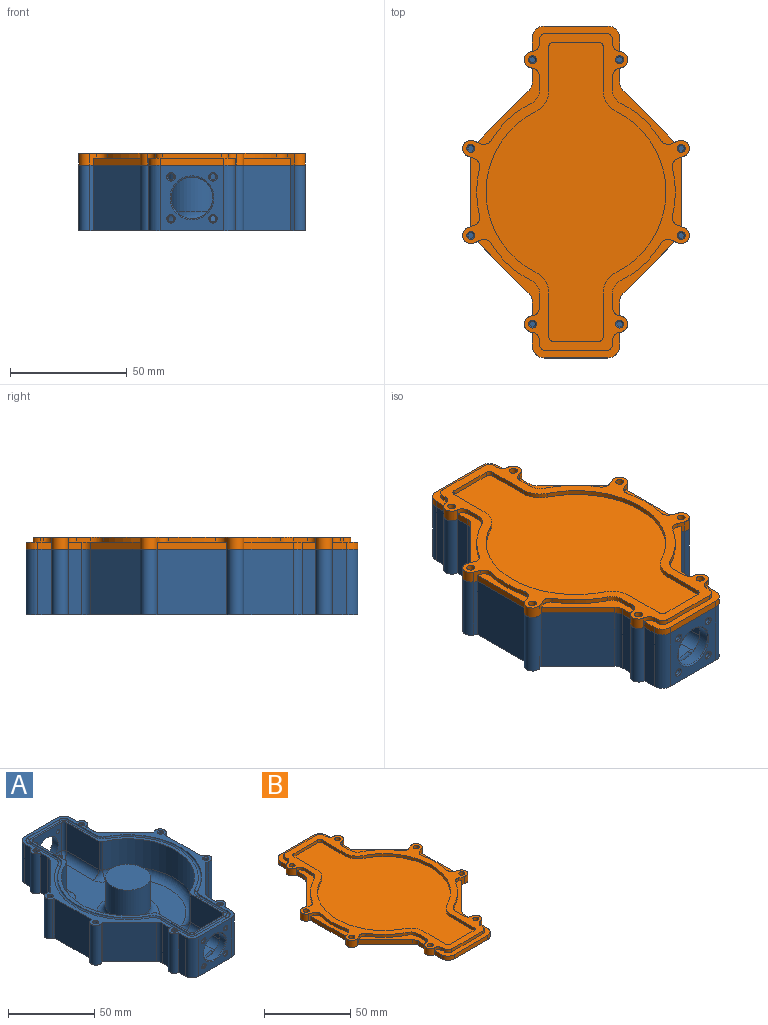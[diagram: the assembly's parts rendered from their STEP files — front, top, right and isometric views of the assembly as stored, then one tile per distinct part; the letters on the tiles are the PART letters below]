
ASSEMBLY  parts=2 mates=1
PART A: 143 faces, bbox 97x142x28.5 mm
  f0: plane 134.24x81.24mm, normal (0,0,1), area 612.3mm2, adj f1,f2,f3,f4,f5,f6,f7,f8
  f1: cylinder r=2mm len=20mm, axis (0,0,1), area 47mm2, adj f0,f2,f16,f140
  f2: plane 26.64x20mm, normal (-1,0,0), area 532.8mm2, adj f0,f1,f3,f138
  f3: cylinder r=2mm len=20mm, axis (0,0,1), area 62.8mm2, adj f0,f2,f4,f136
  f4: plane 23.28x20mm, normal (0,-1,0), area 232.5mm2, adj f0,f3,f5,f99,f101,f103,f130,f134
  f5: cylinder r=2mm len=20mm, axis (0,0,1), area 62.8mm2, adj f0,f4,f6,f128
  f6: plane 26.64x20mm, normal (1,0,0), area 532.8mm2, adj f0,f5,f7,f126
  f7: cylinder r=2mm len=20mm, axis (0,0,1), area 47mm2, adj f0,f6,f8,f124
  f8: cylinder r=38.5mm len=71.03mm, axis (0,0,1), area 1808.5mm2, adj f0,f7,f9,f122
  f9: cylinder r=2mm len=20mm, axis (0,0,1), area 47mm2, adj f0,f8,f10,f123
  f10: plane 26.64x20mm, normal (1,0,0), area 532.8mm2, adj f0,f9,f11,f125
  f11: cylinder r=2mm len=20mm, axis (0,0,1), area 62.8mm2, adj f0,f10,f12,f127
  f12: plane 23.28x20mm, normal (0,1,0), area 232.5mm2, adj f0,f11,f13,f94,f96,f98,f129,f133
  f13: cylinder r=2mm len=20mm, axis (0,0,1), area 62.8mm2, adj f0,f12,f14,f135
  f14: plane 26.64x20mm, normal (-1,0,0), area 532.8mm2, adj f0,f13,f15,f137
  f15: cylinder r=2mm len=20mm, axis (0,0,1), area 47mm2, adj f0,f14,f16,f139
  f16: cylinder r=38.5mm len=71.03mm, axis (0,0,1), area 1808.5mm2, adj f0,f1,f15,f141
  f17: cylinder r=13mm len=26mm, axis (0,0,1), area 1633.6mm2, adj f19,f142
  f18: plane 123.86x67mm, normal (0,0,1), area 3500.3mm2, adj f122,f123,f124,f125,f126,f129,f130,f131
  f19: plane 26x26mm, normal (0,0,1), area 530.9mm2, adj f17
  f20: torus R=6mm, axis (0,0,-1), area 23.3mm2, adj f0,f21,f35,f93
  f21: cylinder r=1mm len=22.75mm, axis (0,-1,0), area 80.6mm2, adj f0,f20,f22,f93
  f22: torus R=3mm, axis (0,0,1), area 16.7mm2, adj f0,f21,f23,f93
  f23: cylinder r=1mm len=25.48mm, axis (-1,0,0), area 90.3mm2, adj f0,f22,f24,f93
  f24: torus R=3mm, axis (0,0,1), area 16.7mm2, adj f0,f23,f25,f93
  f25: cylinder r=1mm len=22.75mm, axis (0,1,0), area 80.6mm2, adj f0,f24,f26,f93
  f26: torus R=6mm, axis (0,0,-1), area 23.3mm2, adj f0,f25,f27,f93
  f27: torus R=41.6mm, axis (0,0,1), area 323.3mm2, adj f0,f26,f28,f93
  f28: torus R=6mm, axis (0,0,-1), area 23.3mm2, adj f0,f27,f29,f93
  f29: cylinder r=1mm len=22.75mm, axis (0,1,0), area 80.6mm2, adj f0,f28,f30,f93
  f30: torus R=3mm, axis (0,0,1), area 16.7mm2, adj f0,f29,f31,f93
  f31: cylinder r=1mm len=25.48mm, axis (1,0,0), area 90.3mm2, adj f0,f30,f32,f93
  f32: torus R=3mm, axis (0,0,1), area 16.7mm2, adj f0,f31,f33,f93
  f33: cylinder r=1mm len=22.75mm, axis (0,-1,0), area 80.6mm2, adj f0,f32,f34,f93
  f34: torus R=6mm, axis (0,0,-1), area 23.3mm2, adj f0,f33,f35,f93
  f35: torus R=41.6mm, axis (0,0,1), area 323.3mm2, adj f0,f20,f34,f93
  f36: plane 2.6x2.6mm, normal (0,0,1), area 5.3mm2, adj f45
  f37: plane 2.6x2.6mm, normal (0,0,1), area 5.3mm2, adj f46
  f38: plane 2.6x2.6mm, normal (0,0,1), area 5.3mm2, adj f47
  f39: plane 2.6x2.6mm, normal (0,0,1), area 5.3mm2, adj f48
  f40: plane 2.6x2.6mm, normal (0,0,1), area 5.3mm2, adj f49
  f41: plane 2.6x2.6mm, normal (0,0,1), area 5.3mm2, adj f50
  f42: plane 2.6x2.6mm, normal (0,0,1), area 5.3mm2, adj f51
  f43: plane 2.6x2.6mm, normal (0,0,1), area 5.3mm2, adj f52
  f44: plane 142x97mm, normal (0,0,-1), area 8803.7mm2, adj f53,f54,f55,f56,f57,f58,f59,f60
  f45: cylinder r=1.3mm len=19.5mm, axis (0,0,1), area 159.3mm2, adj f36,f120
  f46: cylinder r=1.3mm len=19.5mm, axis (0,0,1), area 159.3mm2, adj f37,f119
  f47: cylinder r=1.3mm len=19.5mm, axis (0,0,1), area 159.3mm2, adj f38,f118
  f48: cylinder r=1.3mm len=19.5mm, axis (0,0,1), area 159.3mm2, adj f39,f117
  f49: cylinder r=1.3mm len=19.5mm, axis (0,0,1), area 159.3mm2, adj f40,f114
  f50: cylinder r=1.3mm len=19.5mm, axis (0,0,1), area 159.3mm2, adj f41,f115
  f51: cylinder r=1.3mm len=19.5mm, axis (0,0,1), area 159.3mm2, adj f42,f116
  f52: cylinder r=1.3mm len=19.5mm, axis (0,0,1), area 159.3mm2, adj f43,f121
  f53: plane 29.7x28mm, normal (1,0,0), area 831.7mm2, adj f44,f54,f92,f93
  f54: plane 28x1.34mm, normal (0.38,0.92,0), area 40.6mm2, adj f44,f53,f55,f93
  f55: cylinder r=3.5mm len=28mm, axis (0,0,-1), area 307.9mm2, adj f44,f54,f56,f93
  f56: plane 28x1.34mm, normal (-0.38,-0.92,0), area 40.6mm2, adj f44,f55,f57,f93
  f57: plane 28x22.22mm, normal (0.71,-0.71,0), area 879.8mm2, adj f44,f56,f58,f93
  f58: cylinder r=5mm len=28mm, axis (0,0,-1), area 110mm2, adj f44,f57,f59,f93
  f59: plane 28x5.96mm, normal (1,0,0), area 167mm2, adj f44,f58,f60,f93
  f60: cylinder r=3.5mm len=28mm, axis (0,0,-1), area 307.9mm2, adj f44,f59,f61,f93
  f61: plane 28x5.96mm, normal (1,0,0), area 167mm2, adj f44,f60,f62,f93
  f62: cylinder r=5mm len=28mm, axis (0,0,-1), area 219.9mm2, adj f44,f61,f63,f93
  f63: plane 28x27.28mm, normal (0,-1,0), area 445.5mm2, adj f44,f62,f64,f93,f109,f110,f111,f112
  f64: cylinder r=5mm len=28mm, axis (0,0,-1), area 219.9mm2, adj f44,f63,f65,f93
  f65: plane 28x5.96mm, normal (-1,0,0), area 167mm2, adj f44,f64,f66,f93
  f66: cylinder r=3.5mm len=28mm, axis (0,0,-1), area 307.9mm2, adj f44,f65,f67,f93
  f67: plane 28x5.96mm, normal (-1,0,0), area 167mm2, adj f44,f66,f68,f93
  f68: cylinder r=5mm len=28mm, axis (0,0,-1), area 110mm2, adj f44,f67,f69,f93
  f69: plane 28x22.22mm, normal (-0.71,-0.71,0), area 879.8mm2, adj f44,f68,f70,f93
  f70: plane 28x1.34mm, normal (0.38,-0.92,0), area 40.6mm2, adj f44,f69,f71,f93
  f71: cylinder r=3.5mm len=28mm, axis (0,0,-1), area 307.9mm2, adj f44,f70,f72,f93
  f72: plane 28x1.34mm, normal (-0.38,0.92,0), area 40.6mm2, adj f44,f71,f73,f93
  f73: plane 29.7x28mm, normal (-1,0,0), area 831.7mm2, adj f44,f72,f74,f93
  f74: plane 28x1.34mm, normal (-0.38,-0.92,0), area 40.6mm2, adj f44,f73,f75,f93
  f75: cylinder r=3.5mm len=28mm, axis (0,0,-1), area 307.9mm2, adj f44,f74,f76,f93
  f76: plane 28x1.34mm, normal (0.38,0.92,0), area 40.6mm2, adj f44,f75,f77,f93
  f77: plane 28x22.22mm, normal (-0.71,0.71,0), area 879.8mm2, adj f44,f76,f78,f93
  f78: cylinder r=5mm len=28mm, axis (0,0,-1), area 110mm2, adj f44,f77,f79,f93
  f79: plane 28x5.96mm, normal (-1,0,0), area 167mm2, adj f44,f78,f80,f93
  f80: cylinder r=3.5mm len=28mm, axis (0,0,-1), area 307.9mm2, adj f44,f79,f81,f93
  f81: plane 28x5.96mm, normal (-1,0,0), area 167mm2, adj f44,f80,f82,f93
  f82: cylinder r=5mm len=28mm, axis (0,0,-1), area 219.9mm2, adj f44,f81,f83,f93
  f83: plane 28x27.28mm, normal (0,1,0), area 445.5mm2, adj f44,f82,f84,f93,f104,f105,f106,f107
  f84: cylinder r=5mm len=28mm, axis (0,0,-1), area 219.9mm2, adj f44,f83,f85,f93
  f85: plane 28x5.96mm, normal (1,0,0), area 167mm2, adj f44,f84,f86,f93
  f86: cylinder r=3.5mm len=28mm, axis (0,0,-1), area 307.9mm2, adj f44,f85,f87,f93
  f87: plane 28x5.96mm, normal (1,0,0), area 167mm2, adj f44,f86,f88,f93
  f88: cylinder r=5mm len=28mm, axis (0,0,-1), area 110mm2, adj f44,f87,f89,f93
  f89: plane 28x22.22mm, normal (0.71,0.71,0), area 879.8mm2, adj f44,f88,f90,f93
  f90: plane 28x1.34mm, normal (-0.38,0.92,0), area 40.6mm2, adj f44,f89,f91,f93
  f91: cylinder r=3.5mm len=28mm, axis (0,0,-1), area 307.9mm2, adj f44,f90,f92,f93
  f92: plane 28x1.34mm, normal (0.38,-0.92,0), area 40.6mm2, adj f44,f53,f91,f93
  f93: plane 142x97mm, normal (0,0,1), area 1186.1mm2, adj f20,f21,f22,f23,f24,f25,f26,f27
  f94: cylinder r=1.3mm len=4.5mm, axis (0,-1,0), area 36.8mm2, adj f12,f113
  f95: cylinder r=1.3mm len=6.92mm, axis (0,-1,0), area 46.3mm2, adj f110,f129
  f96: cylinder r=8.9mm len=17.8mm, axis (0,-1,0), area 251.6mm2, adj f12,f109,f131
  f97: cylinder r=1.3mm len=6.92mm, axis (0,-1,0), area 46.3mm2, adj f111,f133
  f98: cylinder r=1.3mm len=4.5mm, axis (0,-1,0), area 36.8mm2, adj f12,f112
  f99: cylinder r=1.3mm len=4.5mm, axis (0,1,0), area 36.8mm2, adj f4,f108
  f100: cylinder r=1.3mm len=6.92mm, axis (0,1,0), area 46.3mm2, adj f105,f134
  f101: cylinder r=8.9mm len=17.8mm, axis (0,1,0), area 251.6mm2, adj f4,f104,f132
  f102: cylinder r=1.3mm len=6.92mm, axis (0,1,0), area 46.3mm2, adj f106,f130
  f103: cylinder r=1.3mm len=4.5mm, axis (0,1,0), area 36.8mm2, adj f4,f107
  f104: torus R=9.4mm, axis (0,1,0), area 44.8mm2, adj f83,f101
  f105: torus R=1.8mm, axis (0,1,0), area 7.3mm2, adj f83,f100
  f106: torus R=1.8mm, axis (0,1,0), area 7.3mm2, adj f83,f102
  f107: torus R=1.8mm, axis (0,1,0), area 7.3mm2, adj f83,f103
  f108: torus R=1.8mm, axis (0,1,0), area 7.3mm2, adj f83,f99
  f109: torus R=9.4mm, axis (0,1,0), area 44.8mm2, adj f63,f96
  f110: torus R=1.8mm, axis (0,1,0), area 7.3mm2, adj f63,f95
  f111: torus R=1.8mm, axis (0,1,0), area 7.3mm2, adj f63,f97
  f112: torus R=1.8mm, axis (0,1,0), area 7.3mm2, adj f63,f98
  f113: torus R=1.8mm, axis (0,1,0), area 7.3mm2, adj f63,f94
  f114: torus R=1.8mm, axis (0,0,1), area 7.3mm2, adj f49,f93
  f115: torus R=1.8mm, axis (0,0,1), area 7.3mm2, adj f50,f93
  f116: torus R=1.8mm, axis (0,0,1), area 7.3mm2, adj f51,f93
  f117: torus R=1.8mm, axis (0,0,1), area 7.3mm2, adj f48,f93
  f118: torus R=1.8mm, axis (0,0,1), area 7.3mm2, adj f47,f93
  f119: torus R=1.8mm, axis (0,0,1), area 7.3mm2, adj f46,f93
  f120: torus R=1.8mm, axis (0,0,1), area 7.3mm2, adj f45,f93
  f121: torus R=1.8mm, axis (0,0,1), area 7.3mm2, adj f52,f93
  f122: torus R=33.5mm, axis (0,0,1), area 676.7mm2, adj f8,f18,f123,f124
  f123: torus R=7mm, axis (0,0,1), area 35.2mm2, adj f9,f18,f122,f125
  f124: torus R=7mm, axis (0,0,1), area 35.2mm2, adj f7,f18,f122,f126
  f125: cylinder r=5mm len=26.64mm, axis (0,-1,0), area 197.5mm2, adj f10,f18,f123,f127
  f126: cylinder r=5mm len=26.64mm, axis (0,-1,0), area 197.5mm2, adj f6,f18,f124,f128
  f127: bspline ~5.91x5mm, area 16.7mm2, adj f11,f125,f129
  f128: bspline ~5.91x5mm, area 16.7mm2, adj f5,f126,f130
  f129: cylinder r=5mm len=5.07mm, axis (1,0,0), area 21.1mm2, adj f12,f18,f95,f127,f131
  f130: cylinder r=5mm len=5.07mm, axis (-1,0,0), area 21.1mm2, adj f4,f18,f102,f128,f132
  f131: bspline ~13.15x5mm, area 76.6mm2, adj f18,f96,f129,f133
  f132: bspline ~13.15x5mm, area 76.6mm2, adj f18,f101,f130,f134
  f133: cylinder r=5mm len=5.07mm, axis (1,0,0), area 21.1mm2, adj f12,f18,f97,f131,f135
  f134: cylinder r=5mm len=5.07mm, axis (-1,0,0), area 21.1mm2, adj f4,f18,f100,f132,f136
  f135: bspline ~5.91x5mm, area 16.7mm2, adj f13,f133,f137
  f136: bspline ~5.91x5mm, area 16.7mm2, adj f3,f134,f138
  f137: cylinder r=5mm len=26.64mm, axis (0,1,0), area 197.5mm2, adj f14,f18,f135,f139
  f138: cylinder r=5mm len=26.64mm, axis (0,1,0), area 197.5mm2, adj f2,f18,f136,f140
  f139: torus R=7mm, axis (0,0,1), area 35.2mm2, adj f15,f18,f137,f141
  f140: torus R=7mm, axis (0,0,1), area 35.2mm2, adj f1,f18,f138,f141
  f141: torus R=33.5mm, axis (0,0,1), area 676.7mm2, adj f16,f18,f139,f140
  f142: torus R=18mm, axis (0,0,1), area 731.2mm2, adj f17,f18
PART B: 115 faces, bbox 97x142x5 mm
  f0: plane 37.28x10.95mm, normal (0,0,1), area 147.6mm2, adj f1,f3,f29,f30,f31,f32,f33,f68
  f1: plane 2x1.48mm, normal (1,0,0), area 3mm2, adj f0,f53,f70,f100
  f2: cylinder r=3.5mm len=6.98mm, axis (0,0,-1), area 52.5mm2, adj f52,f53,f99,f100
  f3: plane 2x1.48mm, normal (-1,0,0), area 3mm2, adj f0,f53,f68,f102
  f4: cylinder r=3.5mm len=6.98mm, axis (0,0,-1), area 52.5mm2, adj f52,f53,f101,f102
  f5: plane 32.65x26.68mm, normal (0,0,1), area 138mm2, adj f6,f17,f45,f46,f47,f73,f87,f104
  f6: plane 6.15x2mm, normal (1,0,0), area 12.3mm2, adj f5,f53,f73,f104
  f7: cylinder r=3.5mm len=6.98mm, axis (0,0,-1), area 52.5mm2, adj f52,f53,f103,f104
  f8: plane 32.65x26.68mm, normal (0,0,1), area 138mm2, adj f9,f11,f12,f38,f39,f77,f90,f106
  f9: plane 6.15x2mm, normal (-1,0,0), area 12.3mm2, adj f8,f53,f77,f106
  f10: cylinder r=3.5mm len=6.98mm, axis (0,0,-1), area 52.5mm2, adj f52,f53,f105,f106
  f11: plane 22.22x22.22mm, normal (-0.71,-0.71,0), area 94.3mm2, adj f8,f38,f52,f90
  f12: cylinder r=42.5mm len=17.37mm, axis (0,0,1), area 47.8mm2, adj f8,f53,f77,f108
  f13: plane 29.7x3.82mm, normal (0,0,1), area 86.9mm2, adj f14,f15,f86,f88,f110,f112
  f14: plane 29.7x3mm, normal (1,0,0), area 89.1mm2, adj f13,f52,f86,f88
  f15: cylinder r=42.5mm len=20.2mm, axis (0,0,1), area 40.8mm2, adj f13,f53,f110,f112
  f16: cylinder r=3.5mm len=6.73mm, axis (0,0,-1), area 55mm2, adj f52,f53,f85,f86
  f17: cylinder r=42.5mm len=17.37mm, axis (0,0,1), area 47.8mm2, adj f5,f53,f73,f109
  f18: plane 32.65x26.68mm, normal (0,0,1), area 138mm2, adj f19,f21,f25,f34,f35,f67,f84,f101
  f19: plane 22.22x22.22mm, normal (-0.71,0.71,0), area 94.3mm2, adj f18,f35,f52,f84
  f20: cylinder r=3.5mm len=6.73mm, axis (0,0,-1), area 55mm2, adj f52,f53,f83,f84
  f21: cylinder r=42.5mm len=17.37mm, axis (0,0,1), area 47.8mm2, adj f18,f53,f67,f114
  f22: plane 32.65x26.68mm, normal (0,0,1), area 138mm2, adj f23,f49,f50,f51,f71,f72,f85,f99
  f23: plane 6.15x2mm, normal (1,0,0), area 12.3mm2, adj f22,f53,f71,f99
  f24: plane 29.7x3.82mm, normal (0,0,1), area 86.9mm2, adj f36,f66,f83,f89,f107,f113
  f25: plane 6.15x2mm, normal (-1,0,0), area 12.3mm2, adj f18,f53,f67,f101
  f26: plane 37.28x10.95mm, normal (0,0,1), area 147.6mm2, adj f27,f28,f40,f41,f42,f43,f44,f74
  f27: plane 2x1.48mm, normal (-1,0,0), area 3mm2, adj f26,f53,f76,f105
  f28: plane 2x1.48mm, normal (1,0,0), area 3mm2, adj f26,f53,f74,f103
  f29: plane 5.95x3mm, normal (1,0,0), area 17.8mm2, adj f0,f30,f52,f100
  f30: cylinder r=5mm len=5mm, axis (0,0,-1), area 23.6mm2, adj f0,f29,f31,f52
  f31: plane 27.28x3mm, normal (0,1,0), area 81.8mm2, adj f0,f30,f32,f52
  f32: cylinder r=5mm len=5mm, axis (0,0,-1), area 23.6mm2, adj f0,f31,f33,f52
  f33: plane 5.95x3mm, normal (-1,0,0), area 17.8mm2, adj f0,f32,f52,f102
  f34: plane 5.95x3mm, normal (-1,0,0), area 17.8mm2, adj f18,f35,f52,f101
  f35: cylinder r=5mm len=3.54mm, axis (0,0,-1), area 11.8mm2, adj f18,f19,f34,f52
  f36: plane 29.7x3mm, normal (-1,0,0), area 89.1mm2, adj f24,f52,f83,f89
  f37: cylinder r=3.5mm len=6.73mm, axis (0,0,-1), area 55mm2, adj f52,f53,f89,f90
  f38: cylinder r=5mm len=3.54mm, axis (0,0,-1), area 11.8mm2, adj f8,f11,f39,f52
  f39: plane 5.95x3mm, normal (-1,0,0), area 17.8mm2, adj f8,f38,f52,f106
  f40: plane 5.95x3mm, normal (-1,0,0), area 17.8mm2, adj f26,f41,f52,f105
  f41: cylinder r=5mm len=5mm, axis (0,0,-1), area 23.6mm2, adj f26,f40,f42,f52
  f42: plane 27.28x3mm, normal (0,-1,0), area 81.8mm2, adj f26,f41,f43,f52
  f43: cylinder r=5mm len=5mm, axis (0,0,-1), area 23.6mm2, adj f26,f42,f44,f52
  f44: plane 5.95x3mm, normal (1,0,0), area 17.8mm2, adj f26,f43,f52,f103
  f45: plane 5.95x3mm, normal (1,0,0), area 17.8mm2, adj f5,f46,f52,f104
  f46: cylinder r=5mm len=3.54mm, axis (0,0,-1), area 11.8mm2, adj f5,f45,f47,f52
  f47: plane 22.22x22.22mm, normal (0.71,-0.71,0), area 94.3mm2, adj f5,f46,f52,f87
  f48: cylinder r=3.5mm len=6.73mm, axis (0,0,-1), area 55mm2, adj f52,f53,f87,f88
  f49: plane 22.22x22.22mm, normal (0.71,0.71,0), area 94.3mm2, adj f22,f50,f52,f85
  f50: cylinder r=5mm len=3.54mm, axis (0,0,-1), area 11.8mm2, adj f22,f49,f51,f52
  f51: plane 5.95x3mm, normal (1,0,0), area 17.8mm2, adj f22,f50,f52,f99
  f52: plane 142x97mm, normal (0,0,-1), area 8731.1mm2, adj f2,f4,f7,f10,f11,f14,f16,f19
  f53: plane 136x97mm, normal (0,0,1), area 1812mm2, adj f1,f2,f3,f4,f6,f7,f9,f10
  f54: cylinder r=38.5mm len=68.91mm, axis (0,0,1), area 170.7mm2, adj f53,f55,f65,f78
  f55: cylinder r=10mm len=8.95mm, axis (0,0,1), area 22.2mm2, adj f53,f54,f56,f78
  f56: plane 18.6x2mm, normal (1,0,0), area 37.2mm2, adj f53,f55,f78,f79
  f57: plane 19.28x2mm, normal (0,-1,0), area 38.6mm2, adj f53,f78,f79,f80
  f58: plane 18.6x2mm, normal (-1,0,0), area 37.2mm2, adj f53,f59,f78,f80
  f59: cylinder r=10mm len=8.95mm, axis (0,0,1), area 22.2mm2, adj f53,f58,f60,f78
  f60: cylinder r=38.5mm len=68.91mm, axis (0,0,1), area 170.7mm2, adj f53,f59,f61,f78
  f61: cylinder r=10mm len=8.95mm, axis (0,0,1), area 22.2mm2, adj f53,f60,f62,f78
  f62: plane 18.6x2mm, normal (-1,0,0), area 37.2mm2, adj f53,f61,f78,f81
  f63: plane 19.28x2mm, normal (0,1,0), area 38.6mm2, adj f53,f78,f81,f82
  f64: plane 18.6x2mm, normal (1,0,0), area 37.2mm2, adj f53,f65,f78,f82
  f65: cylinder r=10mm len=8.95mm, axis (0,0,1), area 22.2mm2, adj f53,f54,f64,f78
  f66: cylinder r=42.5mm len=20.2mm, axis (0,0,1), area 40.8mm2, adj f24,f53,f107,f113
  f67: cylinder r=6mm len=5.37mm, axis (0,0,1), area 13.3mm2, adj f18,f21,f25,f53
  f68: cylinder r=3mm len=3mm, axis (0,0,1), area 9.4mm2, adj f0,f3,f53,f69
  f69: plane 25.28x2mm, normal (0,1,0), area 50.6mm2, adj f0,f53,f68,f70
  f70: cylinder r=3mm len=3mm, axis (0,0,1), area 9.4mm2, adj f0,f1,f53,f69
  f71: cylinder r=6mm len=5.37mm, axis (0,0,1), area 13.3mm2, adj f22,f23,f53,f72
  f72: cylinder r=42.5mm len=17.37mm, axis (0,0,1), area 47.8mm2, adj f22,f53,f71,f111
  f73: cylinder r=6mm len=5.37mm, axis (0,0,1), area 13.3mm2, adj f5,f6,f17,f53
  f74: cylinder r=3mm len=3mm, axis (0,0,1), area 9.4mm2, adj f26,f28,f53,f75
  f75: plane 25.28x2mm, normal (0,-1,0), area 50.6mm2, adj f26,f53,f74,f76
  f76: cylinder r=3mm len=3mm, axis (0,0,1), area 9.4mm2, adj f26,f27,f53,f75
  f77: cylinder r=6mm len=5.37mm, axis (0,0,1), area 13.3mm2, adj f8,f9,f12,f53
  f78: plane 128x77mm, normal (0,0,1), area 5897.9mm2, adj f54,f55,f56,f57,f58,f59,f60,f61
  f79: cylinder r=2mm len=2mm, axis (0,0,-1), area 6.3mm2, adj f53,f56,f57,f78
  f80: cylinder r=2mm len=2mm, axis (0,0,-1), area 6.3mm2, adj f53,f57,f58,f78
  f81: cylinder r=2mm len=2mm, axis (0,0,-1), area 6.3mm2, adj f53,f62,f63,f78
  f82: cylinder r=2mm len=2mm, axis (0,0,-1), area 6.3mm2, adj f53,f63,f64,f78
  f83: plane 5x3mm, normal (-0.38,-0.92,0), area 10.8mm2, adj f20,f24,f36,f52,f53,f113
  f84: plane 5x3mm, normal (0.38,0.92,0), area 10.8mm2, adj f18,f19,f20,f52,f53,f114
  f85: plane 5x3mm, normal (-0.38,0.92,0), area 10.8mm2, adj f16,f22,f49,f52,f53,f111
  f86: plane 5x3mm, normal (0.38,-0.92,0), area 10.8mm2, adj f13,f14,f16,f52,f53,f112
  f87: plane 5x3mm, normal (-0.38,-0.92,0), area 10.8mm2, adj f5,f47,f48,f52,f53,f109
  f88: plane 5x3mm, normal (0.38,0.92,0), area 10.8mm2, adj f13,f14,f48,f52,f53,f110
  f89: plane 5x3mm, normal (-0.38,0.92,0), area 10.8mm2, adj f24,f36,f37,f52,f53,f107
  f90: plane 5x3mm, normal (0.38,-0.92,0), area 10.8mm2, adj f8,f11,f37,f52,f53,f108
  f91: cylinder r=1.7mm len=5mm, axis (0,0,1), area 53.4mm2, adj f52,f53
  f92: cylinder r=1.7mm len=5mm, axis (0,0,1), area 53.4mm2, adj f52,f53
  f93: cylinder r=1.7mm len=5mm, axis (0,0,1), area 53.4mm2, adj f52,f53
  f94: cylinder r=1.7mm len=5mm, axis (0,0,1), area 53.4mm2, adj f52,f53
  f95: cylinder r=1.7mm len=5mm, axis (0,0,1), area 53.4mm2, adj f52,f53
  f96: cylinder r=1.7mm len=5mm, axis (0,0,1), area 53.4mm2, adj f52,f53
  f97: cylinder r=1.7mm len=5mm, axis (0,0,1), area 53.4mm2, adj f52,f53
  f98: cylinder r=1.7mm len=5mm, axis (0,0,1), area 53.4mm2, adj f52,f53
  f99: cylinder r=3.5mm len=5mm, axis (0,0,-1), area 11.2mm2, adj f2,f22,f23,f51,f52,f53
  f100: cylinder r=3.5mm len=5mm, axis (0,0,-1), area 11.2mm2, adj f0,f1,f2,f29,f52,f53
  f101: cylinder r=3.5mm len=5mm, axis (0,0,-1), area 11.2mm2, adj f4,f18,f25,f34,f52,f53
  f102: cylinder r=3.5mm len=5mm, axis (0,0,-1), area 11.2mm2, adj f0,f3,f4,f33,f52,f53
  f103: cylinder r=3.5mm len=5mm, axis (0,0,-1), area 11.2mm2, adj f7,f26,f28,f44,f52,f53
  f104: cylinder r=3.5mm len=5mm, axis (0,0,-1), area 11.2mm2, adj f5,f6,f7,f45,f52,f53
  f105: cylinder r=3.5mm len=5mm, axis (0,0,-1), area 11.2mm2, adj f10,f26,f27,f40,f52,f53
  f106: cylinder r=3.5mm len=5mm, axis (0,0,-1), area 11.2mm2, adj f8,f9,f10,f39,f52,f53
  f107: cylinder r=3.5mm len=4.07mm, axis (0,0,1), area 9.9mm2, adj f24,f53,f66,f89
  f108: cylinder r=3.5mm len=4.33mm, axis (0,0,1), area 9.9mm2, adj f8,f12,f53,f90
  f109: cylinder r=3.5mm len=4.33mm, axis (0,0,1), area 9.9mm2, adj f5,f17,f53,f87
  f110: cylinder r=3.5mm len=4.07mm, axis (0,0,1), area 9.9mm2, adj f13,f15,f53,f88
  f111: cylinder r=3.5mm len=4.33mm, axis (0,0,1), area 9.9mm2, adj f22,f53,f72,f85
  f112: cylinder r=3.5mm len=4.07mm, axis (0,0,1), area 9.9mm2, adj f13,f15,f53,f86
  f113: cylinder r=3.5mm len=4.07mm, axis (0,0,1), area 9.9mm2, adj f24,f53,f66,f83
  f114: cylinder r=3.5mm len=4.33mm, axis (0,0,1), area 9.9mm2, adj f18,f21,f53,f84
PLACE A t=(26.05,12.22,-34.74)mm
PLACE B t=(26.05,12.22,-6.74)mm
MATE planar A.f52 <-> B.f10  axis (0,0,1) through (7.41,-44.32,-6.74)mm
